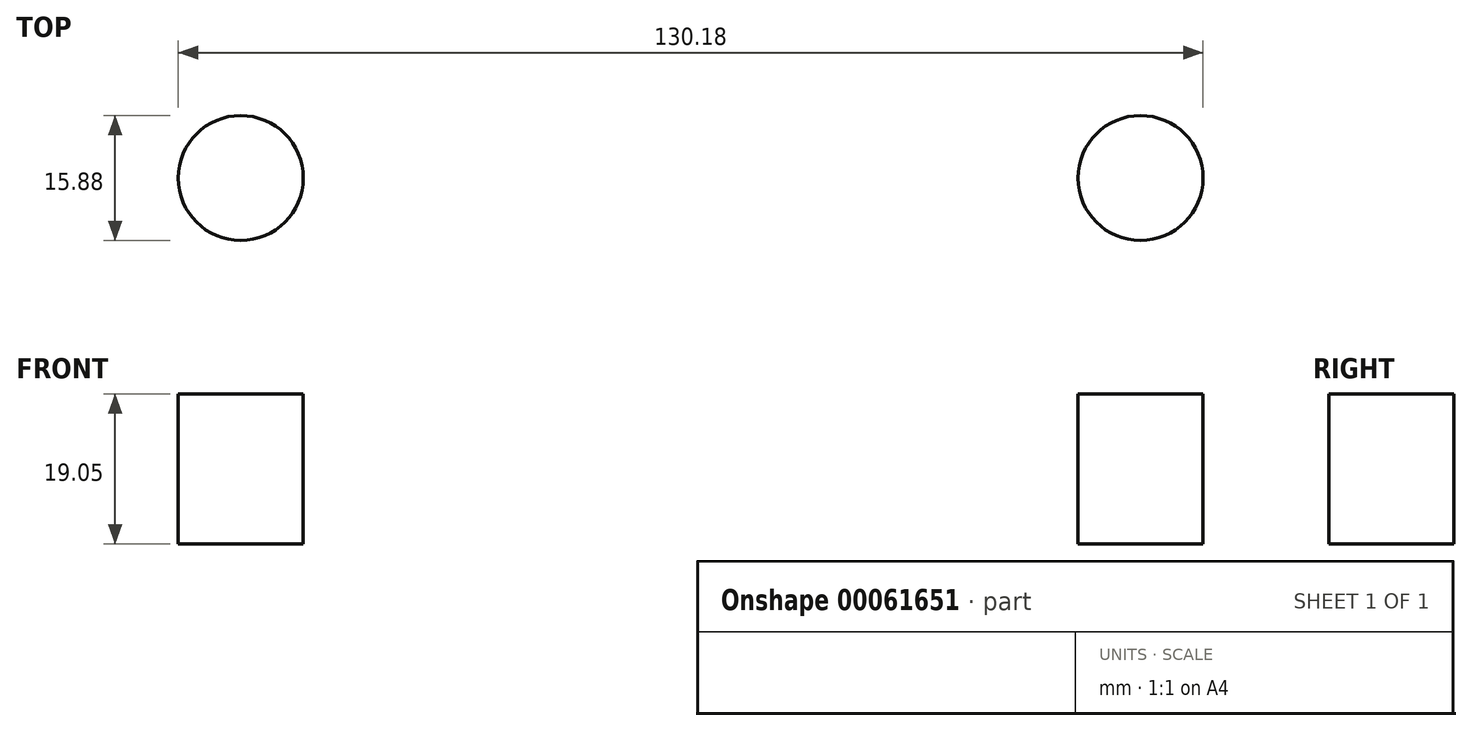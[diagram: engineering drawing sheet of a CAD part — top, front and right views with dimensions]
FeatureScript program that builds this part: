
annotation { "Feature Type Name" : "Feature", "Feature Type Description" : "" }
export const myFeature = defineFeature(function(context is Context, id is Id, definition is map)
    precondition{}
    {
        {
            var Q0;
            Q0=qCreatedBy(makeId("Top.planeOp"),FACE);
            var sketch = newSketch(context, id + "F0", { "sketchPlane" : qUnion([Q0])});
            skLineSegment(sketch, "E0", {"start": v(0, 0) * mm, "end": v(-114.3, 0) * mm, "construction": true});
            skCircle(sketch, "E1", {"center": v(-114.3, 0) * mm, "radius": 7.94 * mm});
            skCircle(sketch, "E2", {"center": v(0, 0) * mm, "radius": 7.94 * mm});
            skSolve(sketch);
        }
        {
            var Q0;
            Q0 = qSketchRegion(id + "F0", true);
            extrude(context, id + "F1", {"entities" : qUnion([Q0]), "oppositeDirection" : true, "depth" : 19.05 * mm});
        }
    });
